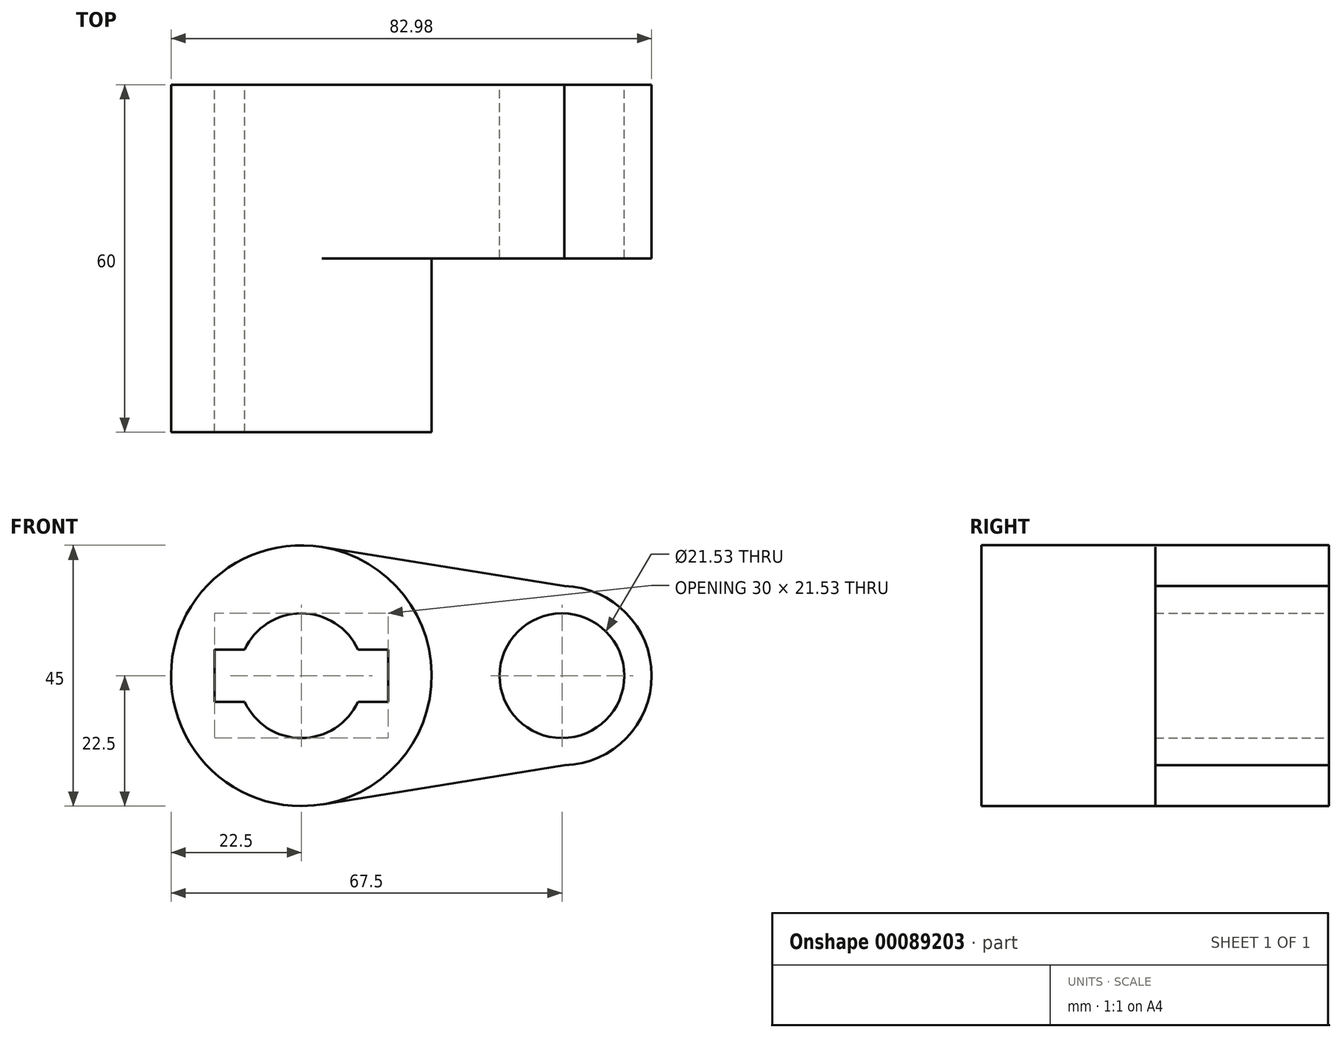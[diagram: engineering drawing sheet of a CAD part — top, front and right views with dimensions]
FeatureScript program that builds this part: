
annotation { "Feature Type Name" : "Feature", "Feature Type Description" : "" }
export const myFeature = defineFeature(function(context is Context, id is Id, definition is map)
    precondition{}
    {
        {
            var Q0;
            Q0=qCreatedBy(makeId("Front.planeOp"),FACE);
            var sketch = newSketch(context, id + "F0", { "sketchPlane" : qUnion([Q0])});
            skCircle(sketch, "E0", {"center": v(0, 0) * mm, "radius": 22.5 * mm});
            skCircle(sketch, "E1", {"center": v(45, 0) * mm, "radius": 15.48 * mm});
            skLineSegment(sketch, "E2", {"start": v(45.4, 15.47) * mm, "end": v(3.58, 22.21) * mm});
            skLineSegment(sketch, "E3", {"start": v(45.45, -15.47) * mm, "end": v(3.58, -22.21) * mm});
            skCircle(sketch, "E4", {"center": v(0, 0) * mm, "radius": 10.77 * mm});
            skCircle(sketch, "E5", {"center": v(45, 0) * mm, "radius": 10.77 * mm});
            skLineSegment(sketch, "E6.bottom", {"start": v(15, 4.5) * mm, "end": v(-15, 4.5) * mm});
            skLineSegment(sketch, "E6.top", {"start": v(15, -4.5) * mm, "end": v(-15, -4.5) * mm});
            skLineSegment(sketch, "E6.left", {"start": v(15, 4.5) * mm, "end": v(15, -4.5) * mm});
            skLineSegment(sketch, "E6.right", {"start": v(-15, 4.5) * mm, "end": v(-15, -4.5) * mm});
            skSolve(sketch);
        }
        {
            var Q0;
            {var subQ0=sQuery(id+"F0.wireOp",EDGE,"E2");Q0=makeQuery(id+"F0.imprint","IMPRINT",FACE,{"disambiguationData":[TD([[makeQuery(id+"F0.imprint","IMPRINT",EDGE,{"derivedFrom":subQ0}),1.0]])]});}
            var Q1;
            Q1=makeQuery(id+"F0.imprint","IMPRINT",FACE,{"disambiguationData":[TD([[makeQuery(id+"F0.imprint","IMPRINT",EDGE,{"derivedFrom":sQuery(id+"F0.wireOp",EDGE,"E5")}),-1.0]])]});
            extrude(context, id + "F1", {"entities" : qUnion([Q0, Q1]), "depth" : 30 * mm});
        }
        {
            var Q0;
            {var subQ11=sQuery(id+"F0.wireOp",EDGE,"E6.left");Q0=makeQuery(id+"F0.imprint","IMPRINT",FACE,{"disambiguationData":[TD([[makeQuery(id+"F0.imprint","IMPRINT",EDGE,{"derivedFrom":subQ11}),1.0]])]});}
            extrude(context, id + "F2", {"entities" : qUnion([Q0]), "operationType" : NewBodyOperationType.ADD, "depth" : 60 * mm});
        }
    });
